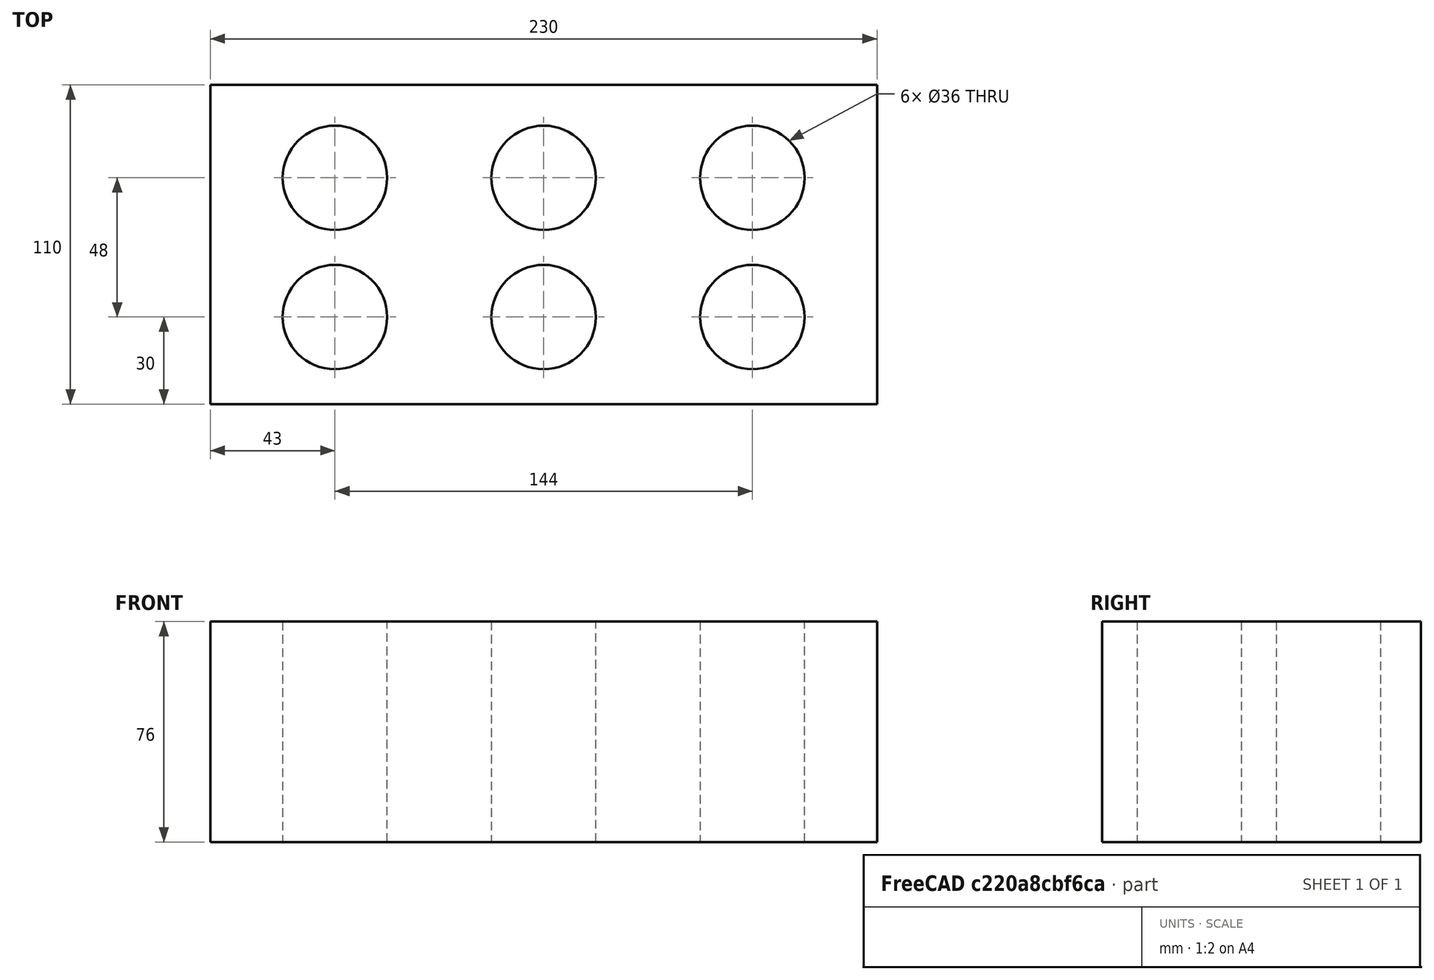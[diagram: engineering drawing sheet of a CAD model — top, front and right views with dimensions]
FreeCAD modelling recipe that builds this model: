
FCSTD DOCUMENT  (FreeCAD 1.0R39319 (Git))
Label: ojt1_t09_r02
License: All rights reserved
LicenseURL: https://en.wikipedia.org/wiki/All_rights_reserved
objects: Part::Cylinder×6, Part::Box×1, Part::MultiFuse×1, Part::Cut×1
note: 9 computed .brp shape members not serialized (recipe doc carries the construction recipe); baked Part::Feature solids carry a one-line shape summary decoded from their .brp

FEATURE [Part::Box] Box  label="Cub"
  AttacherType = Attacher::AttachEngine3D
  Height = 76
  Length = 230
  Width = 110
FEATURE [Part::Cylinder] Cylinder  label="Cilindre"
  Angle = 360
  AttacherType = Attacher::AttachEngine3D
  FirstAngle = 0
  Height = 80
  Placement = pos=(43,30,0) rot=(0,0,1;0rad)
  Radius = 18
  SecondAngle = 0
FEATURE [Part::Cylinder] Cylinder001  label="Cilindre001"
  Angle = 360
  AttacherType = Attacher::AttachEngine3D
  FirstAngle = 0
  Height = 80
  Placement = pos=(43,78,0) rot=(0,0,1;0rad)
  Radius = 18
  SecondAngle = 0
FEATURE [Part::Cylinder] Cylinder002  label="Cilindre002"
  Angle = 360
  AttacherType = Attacher::AttachEngine3D
  FirstAngle = 0
  Height = 80
  Placement = pos=(115,78,0) rot=(0,0,1;0rad)
  Radius = 18
  SecondAngle = 0
FEATURE [Part::Cylinder] Cylinder003  label="Cilindre003"
  Angle = 360
  AttacherType = Attacher::AttachEngine3D
  FirstAngle = 0
  Height = 80
  Placement = pos=(115,30,0) rot=(0,0,1;0rad)
  Radius = 18
  SecondAngle = 0
FEATURE [Part::Cylinder] Cylinder004  label="Cilindre004"
  Angle = 360
  AttacherType = Attacher::AttachEngine3D
  FirstAngle = 0
  Height = 80
  Placement = pos=(187,30,0) rot=(0,0,1;0rad)
  Radius = 18
  SecondAngle = 0
FEATURE [Part::Cylinder] Cylinder005  label="Cilindre005"
  Angle = 360
  AttacherType = Attacher::AttachEngine3D
  FirstAngle = 0
  Height = 80
  Placement = pos=(187,78,0) rot=(0,0,1;0rad)
  Radius = 18
  SecondAngle = 0
FEATURE [Part::MultiFuse] Fusion
  Refine = true
  Shapes = -> [Cylinder,Cylinder001,Cylinder002,Cylinder003,Cylinder004,Cylinder005]
FEATURE [Part::Cut] Cut
  Base = -> Box
  Refine = true
  Tool = -> Fusion
